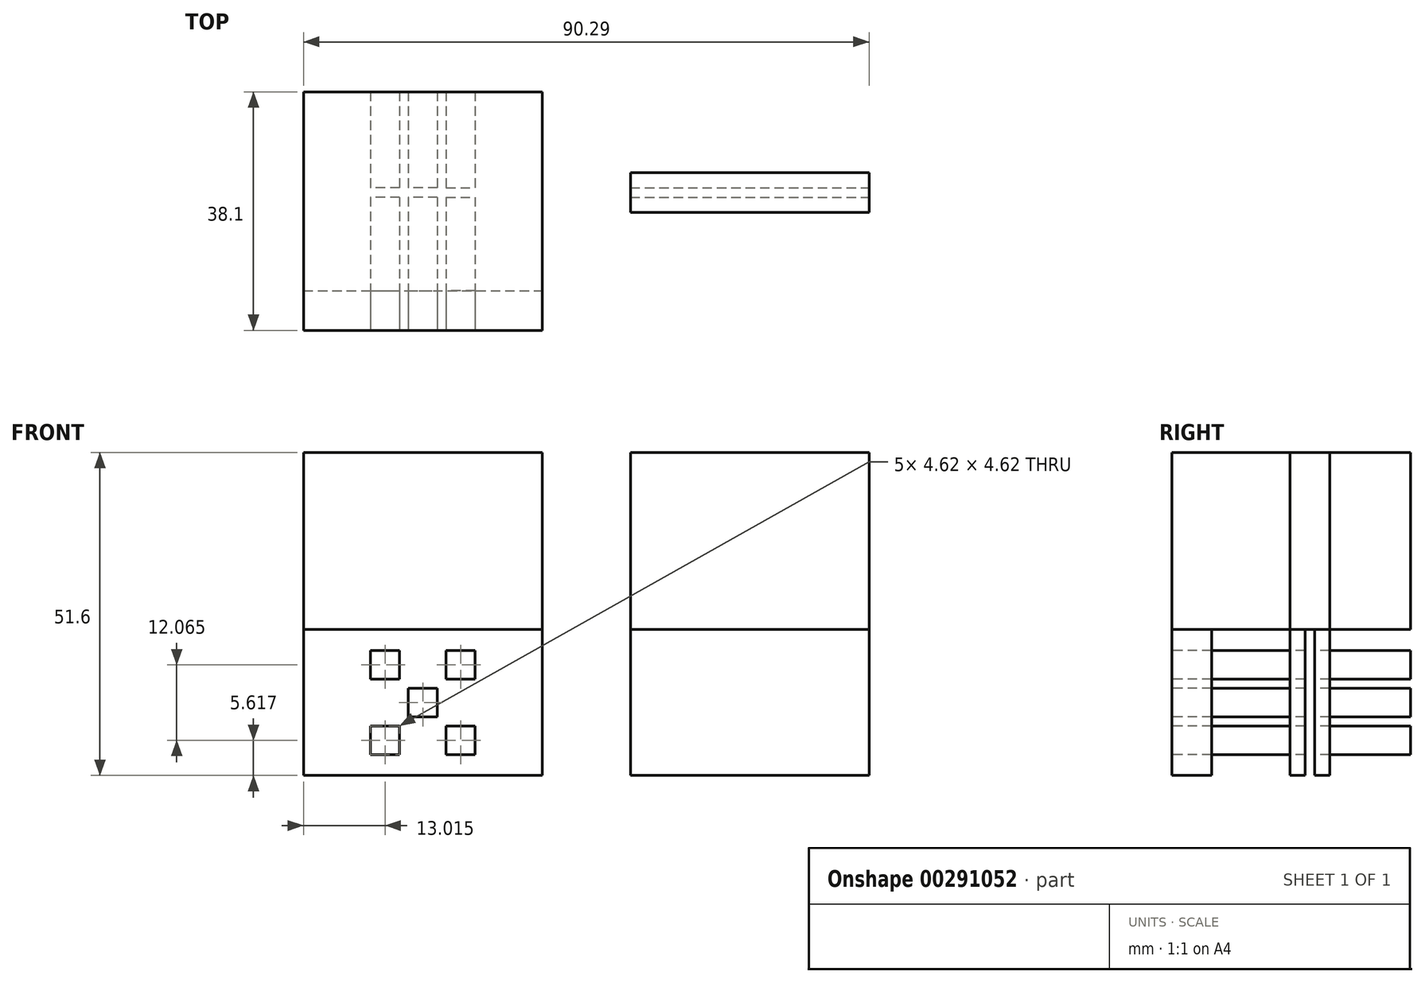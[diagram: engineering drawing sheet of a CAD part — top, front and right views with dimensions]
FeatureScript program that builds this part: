
annotation { "Feature Type Name" : "Feature", "Feature Type Description" : "" }
export const myFeature = defineFeature(function(context is Context, id is Id, definition is map)
    precondition{}
    {
        {
            var Q0;
            Q0=qCreatedBy(makeId("Top.planeOp"),FACE);
            var sketch = newSketch(context, id + "F0", { "sketchPlane" : qUnion([Q0])});
            skLineSegment(sketch, "E0.bottom", {"start": v(-13.84, 24.49) * mm, "end": v(24.26, 24.49) * mm});
            skLineSegment(sketch, "E0.top", {"start": v(-13.84, -13.61) * mm, "end": v(24.26, -13.61) * mm});
            skLineSegment(sketch, "E0.left", {"start": v(-13.84, 24.49) * mm, "end": v(-13.84, -13.61) * mm});
            skLineSegment(sketch, "E0.right", {"start": v(24.26, 24.49) * mm, "end": v(24.26, -13.61) * mm});
            skSolve(sketch);
        }
        {
            var Q0;
            Q0=makeQuery(id+"F0.imprint","IMPRINT",FACE,{"disambiguationData":[TD([[makeQuery(id+"F0.imprint","IMPRINT",EDGE,{"derivedFrom":sQuery(id+"F0.wireOp",EDGE,"E0.bottom")}),-1.0]])]});
            extrude(context, id + "F1", {"entities" : qUnion([Q0]), "depth" : 28.3 * mm});
        }
        {
            var Q0;
            Q0=makeQuery(id+"F1.opExtrude","SWEPT_FACE",FACE,{"disambiguationData":[OSD([sQuery(id+"F0.wireOp",EDGE,"E0.top")])]});
            var sketch = newSketch(context, id + "F2", { "sketchPlane" : qUnion([Q0])});
            skLineSegment(sketch, "E1", {"start": v(24.26, 0) * mm, "end": v(24.26, -23.3) * mm});
            skLineSegment(sketch, "E2", {"start": v(24.26, -23.3) * mm, "end": v(-13.84, -23.3) * mm});
            skLineSegment(sketch, "E3", {"start": v(-13.84, -23.3) * mm, "end": v(-13.84, 0) * mm});
            skLineSegment(sketch, "E4.bottom", {"start": v(-3.14, -3.3) * mm, "end": v(1.49, -3.3) * mm});
            skLineSegment(sketch, "E4.top", {"start": v(-3.14, -7.93) * mm, "end": v(1.49, -7.93) * mm});
            skLineSegment(sketch, "E4.left", {"start": v(-3.14, -3.3) * mm, "end": v(-3.14, -7.93) * mm});
            skLineSegment(sketch, "E4.right", {"start": v(1.49, -3.3) * mm, "end": v(1.49, -7.93) * mm});
            skPoint(sketch, "E5", {"position": v(-0.83, -3.3) * mm});
            skPoint(sketch, "E6", {"position": v(-3.14, -5.62) * mm});
            skPoint(sketch, "E7", {"position": v(11.24, -3.3) * mm});
            skLineSegment(sketch, "E8.bottom", {"start": v(8.93, -3.3) * mm, "end": v(13.55, -3.3) * mm});
            skLineSegment(sketch, "E8.top", {"start": v(8.93, -7.93) * mm, "end": v(13.55, -7.93) * mm});
            skLineSegment(sketch, "E8.left", {"start": v(8.93, -3.3) * mm, "end": v(8.93, -7.93) * mm});
            skLineSegment(sketch, "E8.right", {"start": v(13.55, -3.3) * mm, "end": v(13.55, -7.93) * mm});
            skPoint(sketch, "E9", {"position": v(5.2, -9.34) * mm});
            skLineSegment(sketch, "E10.bottom", {"start": v(2.9, -9.34) * mm, "end": v(7.52, -9.34) * mm});
            skLineSegment(sketch, "E10.top", {"start": v(2.9, -13.96) * mm, "end": v(7.52, -13.96) * mm});
            skLineSegment(sketch, "E10.left", {"start": v(2.9, -9.34) * mm, "end": v(2.9, -13.96) * mm});
            skLineSegment(sketch, "E10.right", {"start": v(7.52, -9.34) * mm, "end": v(7.52, -13.96) * mm});
            skPoint(sketch, "E11.1.0.1", {"position": v(-3.14, -17.68) * mm});
            skLineSegment(sketch, "E11.11.0.1", {"start": v(1.49, -15.37) * mm, "end": v(1.49, -20) * mm});
            skLineSegment(sketch, "E11.14.0.1", {"start": v(-3.14, -20) * mm, "end": v(1.49, -20) * mm});
            skLineSegment(sketch, "E11.22.0.1", {"start": v(-3.14, -15.37) * mm, "end": v(-3.14, -20) * mm});
            skLineSegment(sketch, "E11.25.0.1", {"start": v(-3.14, -15.37) * mm, "end": v(1.49, -15.37) * mm});
            skPoint(sketch, "E12", {"position": v(2.9, -11.65) * mm});
            skPoint(sketch, "E13", {"position": v(5.2, -11.65) * mm});
            skPoint(sketch, "E14", {"position": v(24.26, -11.65) * mm});
            skPoint(sketch, "E15", {"position": v(5.2, 0) * mm});
            skPoint(sketch, "E16", {"position": v(13.55, -5.62) * mm});
            skPoint(sketch, "E17", {"position": v(13.55, -17.68) * mm});
            skPoint(sketch, "E18", {"position": v(7.52, -11.65) * mm});
            skPoint(sketch, "E19", {"position": v(-0.83, -20) * mm});
            skPoint(sketch, "E20", {"position": v(5.2, -13.96) * mm});
            skLineSegment(sketch, "E21.bottom", {"start": v(13.55, -15.37) * mm, "end": v(8.93, -15.37) * mm});
            skLineSegment(sketch, "E21.top", {"start": v(13.55, -20) * mm, "end": v(8.93, -20) * mm});
            skLineSegment(sketch, "E21.left", {"start": v(13.55, -15.37) * mm, "end": v(13.55, -20) * mm});
            skLineSegment(sketch, "E21.right", {"start": v(8.93, -15.37) * mm, "end": v(8.93, -20) * mm});
            skPoint(sketch, "E22", {"position": v(11.24, -20) * mm});
            skSolve(sketch);
        }
        {
            var Q0;
            Q0=makeQuery(id+"F2.imprint","IMPRINT",FACE,{"disambiguationData":[TD([[makeQuery(id+"F2.imprint","IMPRINT",EDGE,{"derivedFrom":sQuery(id+"F2.wireOp",EDGE,"E8.bottom")}),-1.0]])]});
            var Q1;
            Q1=makeQuery(id+"F2.imprint","IMPRINT",FACE,{"disambiguationData":[TD([[makeQuery(id+"F2.imprint","IMPRINT",EDGE,{"derivedFrom":sQuery(id+"F2.wireOp",EDGE,"E4.bottom")}),-1.0]])]});
            var Q2;
            Q2=makeQuery(id+"F2.imprint","IMPRINT",FACE,{"disambiguationData":[TD([[makeQuery(id+"F2.imprint","IMPRINT",EDGE,{"derivedFrom":sQuery(id+"F2.wireOp",EDGE,"E10.bottom")}),-1.0]])]});
            var Q3;
            Q3=makeQuery(id+"F2.imprint","IMPRINT",FACE,{"disambiguationData":[TD([[makeQuery(id+"F2.imprint","IMPRINT",EDGE,{"derivedFrom":sQuery(id+"F2.wireOp",EDGE,"E21.bottom")}),1.0]])]});
            var Q4;
            Q4=makeQuery(id+"F2.imprint","IMPRINT",FACE,{"disambiguationData":[TD([[makeQuery(id+"F2.imprint","IMPRINT",EDGE,{"derivedFrom":sQuery(id+"F2.wireOp",EDGE,"E11.11.0.1")}),-1.0]])]});
            extrude(context, id + "F3", {"entities" : qUnion([Q0, Q1, Q2, Q3, Q4]), "oppositeDirection" : true, "depth" : 38.1 * mm});
        }
        {
            var Q0;
            Q0=makeQuery(id+"F2.imprint","IMPRINT",FACE,{"disambiguationData":[TD([[makeQuery(id+"F2.imprint","IMPRINT",EDGE,{"derivedFrom":sQuery(id+"F2.wireOp",EDGE,"E1")}),-1.0]])]});
            extrude(context, id + "F4", {"entities" : qUnion([Q0]), "oppositeDirection" : true, "depth" : 6.35 * mm});
        }
        {
            var Q0;
            Q0=qCreatedBy(makeId("Top.planeOp"),FACE);
            var sketch = newSketch(context, id + "F5", { "sketchPlane" : qUnion([Q0])});
            skLineSegment(sketch, "E23.bottom", {"start": v(38.35, 11.6) * mm, "end": v(76.45, 11.6) * mm});
            skLineSegment(sketch, "E23.top", {"start": v(38.35, 5.25) * mm, "end": v(76.45, 5.25) * mm});
            skLineSegment(sketch, "E23.left", {"start": v(38.35, 11.6) * mm, "end": v(38.35, 5.25) * mm});
            skLineSegment(sketch, "E23.right", {"start": v(76.45, 11.6) * mm, "end": v(76.45, 5.25) * mm});
            skSolve(sketch);
        }
        {
            var Q0;
            Q0=makeQuery(id+"F5.imprint","IMPRINT",FACE,{"disambiguationData":[TD([[makeQuery(id+"F5.imprint","IMPRINT",EDGE,{"derivedFrom":sQuery(id+"F5.wireOp",EDGE,"E23.bottom")}),-1.0]])]});
            extrude(context, id + "F6", {"entities" : qUnion([Q0]), "oppositeDirection" : true, "depth" : 23.3 * mm});
        }
        {
            var Q0;
            Q0=makeQuery(id+"F6.opExtrude","SWEPT_FACE",FACE,{"disambiguationData":[OSD([sQuery(id+"F5.wireOp",EDGE,"E23.right")])]});
            var sketch = newSketch(context, id + "F7", { "sketchPlane" : qUnion([Q0])});
            skPoint(sketch, "E24", {"position": v(8.42, 0) * mm});
            skLineSegment(sketch, "E25.bottom", {"start": v(7.66, 0) * mm, "end": v(9.19, 0) * mm});
            skLineSegment(sketch, "E25.top", {"start": v(7.66, -23.3) * mm, "end": v(9.19, -23.3) * mm});
            skLineSegment(sketch, "E25.left", {"start": v(7.66, 0) * mm, "end": v(7.66, -23.3) * mm});
            skLineSegment(sketch, "E25.right", {"start": v(9.19, 0) * mm, "end": v(9.19, -23.3) * mm});
            skSolve(sketch);
        }
        {
            var Q0;
            Q0=makeQuery(id+"F7.imprint","IMPRINT",FACE,{"disambiguationData":[TD([[makeQuery(id+"F7.imprint","IMPRINT",EDGE,{"derivedFrom":sQuery(id+"F7.wireOp",EDGE,"E25.bottom")}),1.0]])]});
            extrude(context, id + "F8", {"entities" : qUnion([Q0]), "operationType" : NewBodyOperationType.REMOVE, "endBound" : BoundingType.THROUGH_ALL, "oppositeDirection" : true, "depth" : 25.4 * mm});
        }
        {
            var Q0;
            {var subQ0=sQuery(id+"F5.wireOp",EDGE,"E23.top");var subQ1=sQuery(id+"F5.wireOp",EDGE,"E23.left");var subQ2=sQuery(id+"F5.wireOp",EDGE,"E23.right");Q0=makeQuery(id+"F8.boolean.opBoolean","SPLIT",FACE,{"disambiguationData":[TD([makeQuery(id+"F6.opExtrude","SWEPT_FACE",FACE,{"disambiguationData":[OSD([subQ0])]})])],"derivedFrom":makeQuery(id+"F6.opExtrude","CAP_FACE",FACE,{"disambiguationData":[OSD([sQuery(id+"F5.wireOp",EDGE,"E23.bottom"),subQ0,subQ1,subQ2])],"isStart":true})});}
            var sketch = newSketch(context, id + "F9", { "sketchPlane" : qUnion([Q0])});
            skLineSegment(sketch, "E26.bottom", {"start": v(38.35, 5.25) * mm, "end": v(76.45, 5.25) * mm});
            skLineSegment(sketch, "E26.top", {"start": v(38.35, 11.6) * mm, "end": v(76.45, 11.6) * mm});
            skLineSegment(sketch, "E26.left", {"start": v(38.35, 5.25) * mm, "end": v(38.35, 11.6) * mm});
            skLineSegment(sketch, "E26.right", {"start": v(76.45, 5.25) * mm, "end": v(76.45, 11.6) * mm});
            skSolve(sketch);
        }
        {
            var Q0;
            {var subQ0=sQuery(id+"F9.wireOp",EDGE,"E26.bottom");Q0=makeQuery(id+"F9.imprint","IMPRINT",FACE,{"disambiguationData":[TD([[makeQuery(id+"F9.imprint","IMPRINT",EDGE,{"derivedFrom":subQ0}),1.0]])]});}
            var Q1;
            {var subQ0=sQuery(id+"F9.wireOp",EDGE,"E26.top");Q1=makeQuery(id+"F9.imprint","IMPRINT",FACE,{"disambiguationData":[TD([[makeQuery(id+"F9.imprint","IMPRINT",EDGE,{"derivedFrom":subQ0}),-1.0]])]});}
            extrude(context, id + "F10", {"entities" : qUnion([Q0, Q1]), "depth" : 28.3 * mm});
        }
    });
